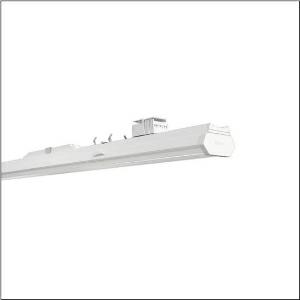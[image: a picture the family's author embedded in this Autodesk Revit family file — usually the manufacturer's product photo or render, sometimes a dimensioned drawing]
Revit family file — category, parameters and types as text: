
# Revit family: licross_21_protected_mo_52tp12dn4a5g
name_source: partatom
category: Lighting Fixtures
units: mm (PartAtom-declared; Revit-internal decimal feet)

## family parameters
Cut with Voids When Loaded = No
Host = Face
Light Source = No
Part Type = Normal
Room Calculation Point = No
Round Connector Dimension = Use Diameter
Shared = No

## types (1)
- --- (1 x LED, 10700 lm, 62 W, 4000K)
    Apparent Load = 62 VA
    CIE Flux Codes = 73 92 98 99 100
    Color Rendering = 80
    Color Temperature = 4000K
    Default Elevation = 1800 mm
    Description = Licross 21 Protected MO, luminaire insert, of sheet steel, galvanised, coil coated, white, length: 1.500mm, width: 90mm, height: 103mm, LED rated luminous flux: 10.700lm, light colour: 840, SDCM (Standard Deviation of Colour Matching)MacAdam ≤ 3 SDCM (initial), control gear: DALI 2, with plug, 5-pole, with phase selection, mains connection: 220..240V, AC, 50/60Hz, rated input power: 62W, internal wiring halogen-free, primary light control with lens, of plastic, primary optical cover: cover, of PMMA, light emission: direct distribution, primary light characteristic: symmetric, protection rating (complete): IP64, insulation class (complete): insulation class I (protective earthing), certification: CE, ENEC, VDE, UKCA, protection symbol: D if used in an environment with conductive dust loads with corresponding accessories, impact resistance: IK06, permissible ambient temperature for indoor applications: -25..+35°C, corresponds to IFS (International Featured Standards) requirements for safety and quality in the food industry, reducing of maximum allowable ambient temperature of 5°C with ceiling mounting, LABS conformity tested according to VDMA 24364:2018-05, The light source and the operating device comply with the requirements of the Ecodesign Regulation (EU) 2019/2020 and are replaceable in accordance with this regulation, packaging unit: 1 piece
    Height = 92 mm
    Lamp = 1 x LED
    Lamp Light Flux = 10700 lm
    Lamp Power = 62 W
    Lamp count = 1
    Length = 1500 mm
    Luminous efficacy = 173 lm/W
    Manufacturer = Siteco
    ModVariant = No
    Model = 52TP12DN4A5G
    Mounting Place = Ceiling
    Mounting Type = Pendant
    Number of Poles = 1
    OnlyDefault = Yes
    Power Factor = 1
    Product Name = Licross 21 Protected MO
    Product group = luminaire insert | ceiling pendant
    ProductGroupID = 901
    Protection Class = Protection class I
    Protection Degree = IP 64
    RLX_Detail_Level = 1
    RLX_Emergency_Light_Flux = 0 lm
    RLX_Emergency_Type = 0
    RLX_Emergency_Type_DB = No
    RlxData = <blob elided: 24777 chars, md5=d81e78ea>
    Socket = socket
    Standby Power = 0 W
    System Light Flux = 10700 lm
    System Power = 62 W
    Type Comments = factory setting: luminous flux: 100 % | dim-lin: 254 | 418 mA
    Type Image = l_1256148.jpg
    URL = http://relux.com
    VarID = @adj_128845
    Voltage = 0 V
    Weight = 0.00 kg
    Width = 88 mm

## geometry (parser evidence)
native form markers: Blend x4, Sweep x9
no freeform markers — native parametric forms only
